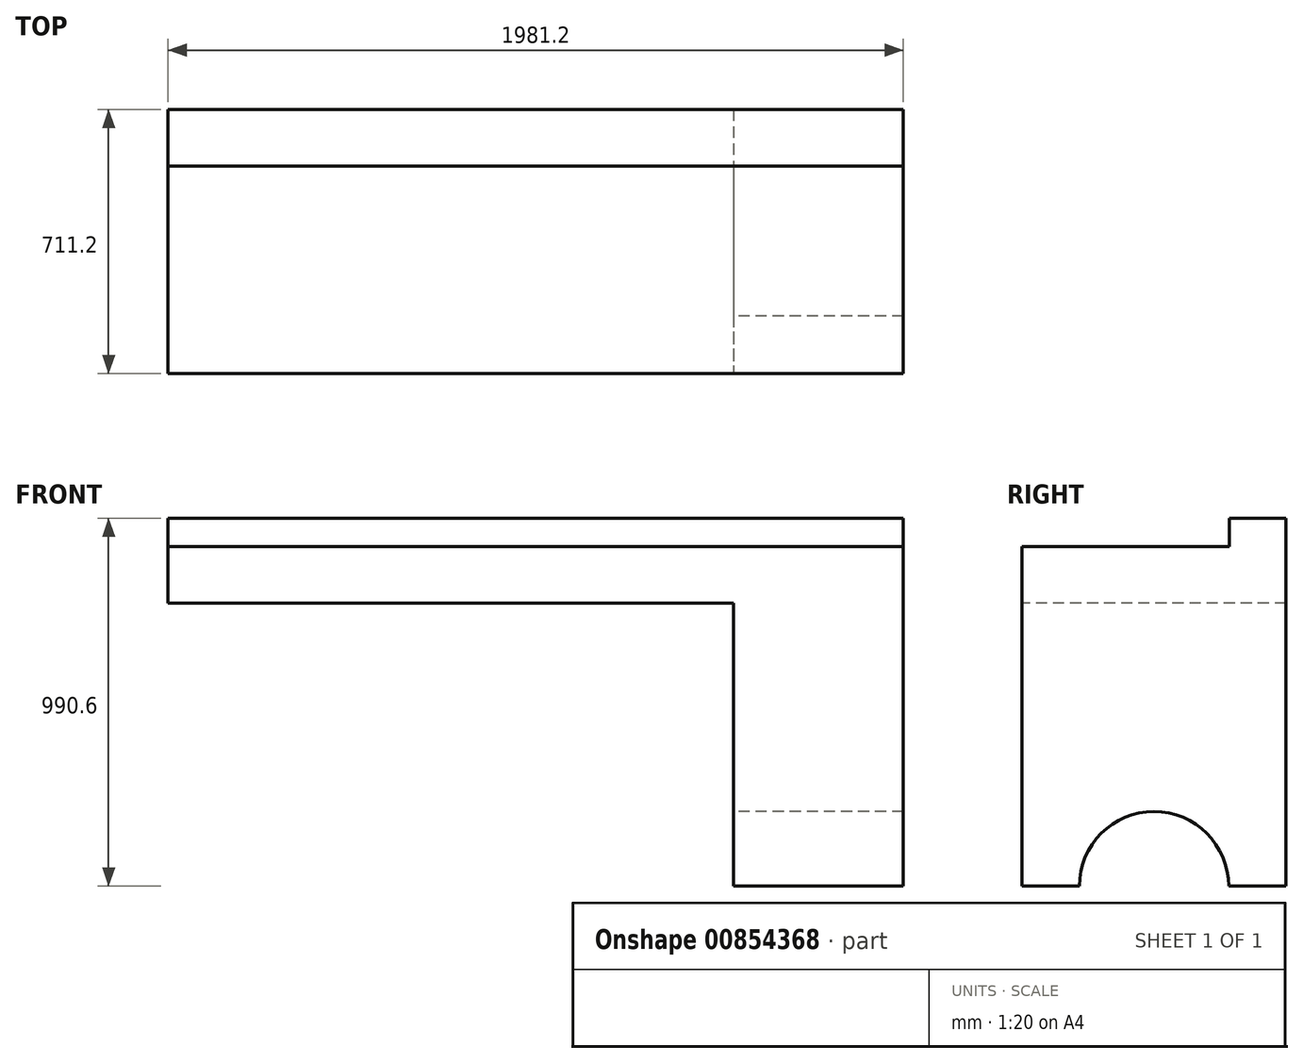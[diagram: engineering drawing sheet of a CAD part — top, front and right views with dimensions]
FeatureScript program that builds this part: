
annotation { "Feature Type Name" : "Feature", "Feature Type Description" : "" }
export const myFeature = defineFeature(function(context is Context, id is Id, definition is map)
    precondition{}
    {
        {
            var Q0;
            Q0=qCreatedBy(makeId("Right.planeOp"),FACE);
            var sketch = newSketch(context, id + "F0", { "sketchPlane" : qUnion([Q0])});
            skLineSegment(sketch, "E0.bottom", {"start": v(-349.9, 713.45) * mm, "end": v(361.3, 713.45) * mm});
            skLineSegment(sketch, "E0.top", {"start": v(-349.9, -200.95) * mm, "end": v(-195.33, -200.95) * mm});
            skLineSegment(sketch, "E0.left", {"start": v(-349.9, 713.45) * mm, "end": v(-349.9, -200.95) * mm});
            skLineSegment(sketch, "E0.right", {"start": v(361.3, 713.45) * mm, "end": v(361.3, -200.95) * mm});
            skLineSegment(sketch, "E1.bottom", {"start": v(361.3, 713.45) * mm, "end": v(208.9, 713.45) * mm});
            skLineSegment(sketch, "E1.top", {"start": v(361.3, 789.65) * mm, "end": v(208.9, 789.65) * mm});
            skLineSegment(sketch, "E1.left", {"start": v(361.3, 713.45) * mm, "end": v(361.3, 789.65) * mm});
            skLineSegment(sketch, "E1.right", {"start": v(208.9, 713.45) * mm, "end": v(208.9, 789.65) * mm});
            skArc(sketch, "E2", {"start": v(206.72, -200.95) * mm, "mid": v(5.7, 0.08) * mm, "end": v(-195.33, -200.95) * mm});
            skLineSegment(sketch, "E3.trimOffspring", {"start": v(206.72, -200.95) * mm, "end": v(361.3, -200.95) * mm});
            skSolve(sketch);
        }
        {
            var Q0;
            Q0=makeQuery(id+"F0.imprint","IMPRINT",FACE,{"disambiguationData":[TD([[makeQuery(id+"F0.imprint","IMPRINT",EDGE,{"derivedFrom":sQuery(id+"F0.wireOp",EDGE,"E0.top")}),1.0]])]});
            var Q1;
            Q1=makeQuery(id+"F0.imprint","IMPRINT",FACE,{"disambiguationData":[TD([[makeQuery(id+"F0.imprint","IMPRINT",EDGE,{"derivedFrom":sQuery(id+"F0.wireOp",EDGE,"E1.top")}),1.0]])]});
            extrude(context, id + "F1", {"entities" : qUnion([Q0, Q1]), "depth" : 1981.2 * mm, "offsetDistance" : 25.4 * mm});
        }
        {
            var Q0;
            Q0=makeQuery(id+"F1.opExtrude","SWEPT_FACE",FACE,{"disambiguationData":[OSD([sQuery(id+"F0.wireOp",EDGE,"E0.left")])]});
            var sketch = newSketch(context, id + "F2", { "sketchPlane" : qUnion([Q0])});
            skLineSegment(sketch, "E4.bottom", {"start": v(0, 713.45) * mm, "end": v(1981.2, 713.45) * mm});
            skLineSegment(sketch, "E4.top", {"start": v(0, 561.05) * mm, "end": v(1981.2, 561.05) * mm});
            skLineSegment(sketch, "E4.left", {"start": v(0, 713.45) * mm, "end": v(0, 561.05) * mm});
            skLineSegment(sketch, "E4.right", {"start": v(1981.2, 713.45) * mm, "end": v(1981.2, 561.05) * mm});
            skLineSegment(sketch, "E5.bottom", {"start": v(0, -200.95) * mm, "end": v(1524, -200.95) * mm});
            skLineSegment(sketch, "E5.top", {"start": v(0, 561.05) * mm, "end": v(1524, 561.05) * mm});
            skLineSegment(sketch, "E5.left", {"start": v(0, -200.95) * mm, "end": v(0, 561.05) * mm});
            skLineSegment(sketch, "E5.right", {"start": v(1524, -200.95) * mm, "end": v(1524, 561.05) * mm});
            skLineSegment(sketch, "E6.bottom", {"start": v(1524, 561.05) * mm, "end": v(-59.06, 561.05) * mm});
            skLineSegment(sketch, "E6.top", {"start": v(1524, -200.95) * mm, "end": v(-59.06, -200.95) * mm});
            skLineSegment(sketch, "E6.left", {"start": v(1524, 561.05) * mm, "end": v(1524, -200.95) * mm});
            skLineSegment(sketch, "E6.right", {"start": v(-59.06, 561.05) * mm, "end": v(-59.06, -200.95) * mm});
            skSolve(sketch);
        }
        {
            var Q0;
            {var subQ0=sQuery(id+"F2.wireOp",EDGE,"E5.left");Q0=makeQuery(id+"F2.imprint","IMPRINT",FACE,{"disambiguationData":[TD([[makeQuery(id+"F2.imprint","IMPRINT",EDGE,{"derivedFrom":subQ0}),-1.0]])]});}
            var Q1;
            {var subQ0=sQuery(id+"F2.wireOp",EDGE,"E5.left");Q1=makeQuery(id+"F2.imprint","IMPRINT",FACE,{"disambiguationData":[TD([[makeQuery(id+"F2.imprint","IMPRINT",EDGE,{"derivedFrom":subQ0}),1.0]])]});}
            extrude(context, id + "F3", {"entities" : qUnion([Q0, Q1]), "operationType" : NewBodyOperationType.REMOVE, "oppositeDirection" : true, "depth" : 711.2 * mm, "offsetDistance" : 25.4 * mm});
        }
    });
